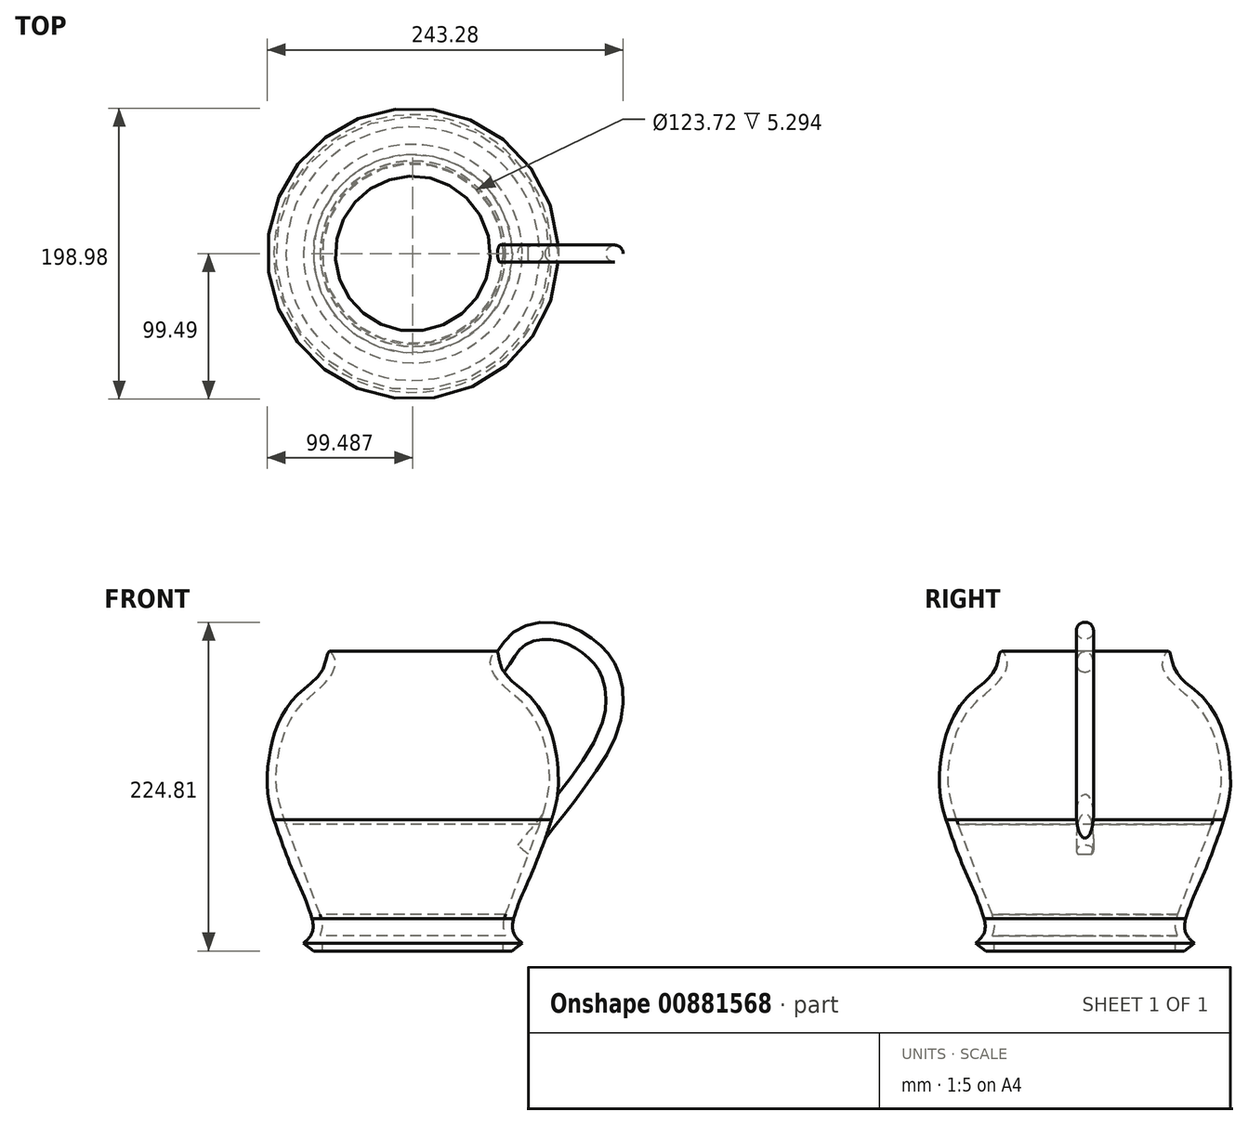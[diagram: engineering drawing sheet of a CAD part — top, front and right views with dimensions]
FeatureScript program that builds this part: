
annotation { "Feature Type Name" : "Feature", "Feature Type Description" : "" }
export const myFeature = defineFeature(function(context is Context, id is Id, definition is map)
    precondition{}
    {
        {
            var Q0;
            Q0=qCreatedBy(makeId("Front.planeOp"),FACE);
            var sketch = newSketch(context, id + "F0", { "sketchPlane" : qUnion([Q0])});
            skLineSegment(sketch, "E0", {"start": v(12.58, -76.87) * mm, "end": v(12.58, 128.13) * mm});
            skLineSegment(sketch, "E1", {"start": v(12.58, -71.58) * mm, "end": v(74.44, -71.58) * mm});
            skLineSegment(sketch, "E2", {"start": v(74.44, -71.58) * mm, "end": v(74.44, -76.87) * mm});
            skLineSegment(sketch, "E3", {"start": v(74.44, -76.87) * mm, "end": v(80.3, -76.87) * mm});
            skLineSegment(sketch, "E4", {"start": v(80.3, -76.87) * mm, "end": v(87.3, -71.58) * mm});
            skLineSegment(sketch, "E5", {"start": v(12.58, -66.58) * mm, "end": v(75.82, -66.58) * mm});
            skLineSegment(sketch, "E6", {"start": v(12.58, -66.58) * mm, "end": v(12.58, -71.58) * mm});
            skLineSegment(sketch, "E7", {"start": v(99.23, 9.61) * mm, "end": v(76, -51.93) * mm});
            skFitSpline(sketch, "E8", {"points": [v(81.48, -54.78) * mm, v(81.48, -64.55) * mm, v(87.3, -71.58) * mm], "startDerivative": vector(-5.47, -19.9) * mm, "endDerivative": vector(14.78, -13.08) * mm});
            skFitSpline(sketch, "E9", {"points": [v(99.23, 9.61) * mm, v(106.1, 41.9) * mm, v(94.34, 84.45) * mm, v(76.45, 102.61) * mm, v(65.53, 120.03) * mm, v(69.78, 128.1) * mm, v(73.83, 116.04) * mm, v(91.23, 98.43) * mm, v(107.09, 72.2) * mm, v(112.06, 39.28) * mm, v(107.53, 12.7) * mm], "startDerivative": vector(84.98, 275.05) * mm, "endDerivative": vector(-101.23, -314) * mm});
            skFitSpline(sketch, "E10", {"points": [v(76, -51.93) * mm, v(74.24, -58.15) * mm, v(75.82, -66.58) * mm], "startDerivative": vector(-3.93, -12.97) * mm, "endDerivative": vector(3.54, -13.69) * mm});
            skFitSpline(sketch, "E11", {"points": [v(107.53, 12.7) * mm, v(94.31, -22.69) * mm, v(81.48, -54.78) * mm], "startDerivative": vector(-25.7, -73.63) * mm, "endDerivative": vector(-18.7, -68.03) * mm});
            skSolve(sketch);
        }
        {
            var Q0;
            Q0=makeQuery(id+"F0.imprint","IMPRINT",FACE,{"disambiguationData":[TD([[makeQuery(id+"F0.imprint","IMPRINT",EDGE,{"derivedFrom":sQuery(id+"F0.wireOp",EDGE,"E1")}),1.0]])]});
            var Q1;
            Q1=sQuery(id+"F0.wireOp",EDGE,"E6");
            revolve(context, id + "F1", {"surfaceOperationType" : NewSurfaceOperationType.NEW, "entities" : qUnion([Q0]), "axis" : qUnion([Q1]), "revolveType" : RevolveType.FULL});
        }
        {
            var Q0;
            Q0=qCreatedBy(makeId("Front.planeOp"),FACE);
            var sketch = newSketch(context, id + "F2", { "sketchPlane" : qUnion([Q0])});
            skFitSpline(sketch, "E12", {"points": [v(89.3, -8.94) * mm, v(117.02, 25.99) * mm, v(149.28, 79.36) * mm, v(147.57, 114.54) * mm, v(135.81, 129.85) * mm, v(112.57, 142.13) * mm, v(84.42, 137.24) * mm, v(69.81, 118.24) * mm], "startDerivative": vector(181.15, 219.3) * mm, "endDerivative": vector(-121.32, -144.01) * mm});
            skSolve(sketch);
        }
        {
            var Q0;
            Q0=sQuery(id+"F2.wireOp",EDGE,"E12");
            var Q1;
            Q1=sQuery(id+"F2.wireOp",VERTEX,"E12.start");
            cPlane(context, id + "F3", {"entities" : qUnion([Q0, Q1]), "cplaneType" : CPlaneType.CURVE_POINT, "offset" : 25 * mm, "width" : 150 * mm, "height" : 150 * mm});
        }
        {
            var Q0;
            Q0=qCreatedBy(id+"F3.planeOp",FACE);
            var sketch = newSketch(context, id + "F4", { "sketchPlane" : qUnion([Q0])});
            skCircle(sketch, "E13", {"center": v(73.65, 0) * mm, "radius": 5.85 * mm});
            skSolve(sketch);
        }
        {
            var Q0;
            Q0=makeQuery(id+"F4.imprint","IMPRINT",FACE,{"disambiguationData":[TD([[makeQuery(id+"F4.imprint","IMPRINT",EDGE,{"derivedFrom":sQuery(id+"F4.wireOp",EDGE,"E13")}),1.0]])]});
            var Q1;
            Q1=sQuery(id+"F2.wireOp",EDGE,"E12");
            sweep(context, id + "F5", {"operationType" : NewBodyOperationType.ADD, "profiles" : qUnion([Q0]), "path" : qUnion([Q1])});
        }
    });
